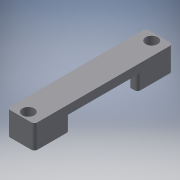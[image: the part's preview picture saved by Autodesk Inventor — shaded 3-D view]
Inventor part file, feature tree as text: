
AUTODESK INVENTOR PART (.ipt)
format: ipt  version: 2018 (Build 220112000, 112)  size: 192,512 bytes
history: native  units: mm
features: reference x4, extrude x3, sketch x3, other x3, projected_geometry x2, plane x1
ambient origin geometry x8: Origin, YZ Plane, XZ Plane, XY Plane, X Axis, Y Axis, Z Axis, Center Point
bodies: Solid1 (feature_tree)
feature tree (16):
  extrude  "Extrusion1"  Depth=5.0mm TaperAngle=0.0deg
  sketch  "Sketch2"  dims[d5=2.75mm d6=2.75mm]
  plane  "Work Plane1"
  extrude  "Extrusion2"  Depth=2.75mm
  extrude  "Extrusion3"  [1 undecoded]
  sketch  "Sketch1"  dims[d0=5.0mm d1=0.0mm d2=5.0mm d3=0.0mm]
  reference  "Reference1"
  reference  "Reference2"
  projected_geometry  "Projected Loop1"
  projected_geometry  "Projected Loop2"
  sketch  "Sketch3"  dims[d7=100.0mm d8=0.0mm]
  reference  "Reference3"
  reference  "Reference4"
  other  "<userpath>\OneDrive\Documents\Inventor\TSA\2018\Animatronics\Tortoise\TurtleAssembly2.iam"
  other  "TurtleAssembly2.iam"
  other  "TablePt2:3"
note: 1 required parameter value undecoded (feature->parameter linkage not recoverable at this tier; creation-order binding heuristic only, values carry confidence <= 0.55)
